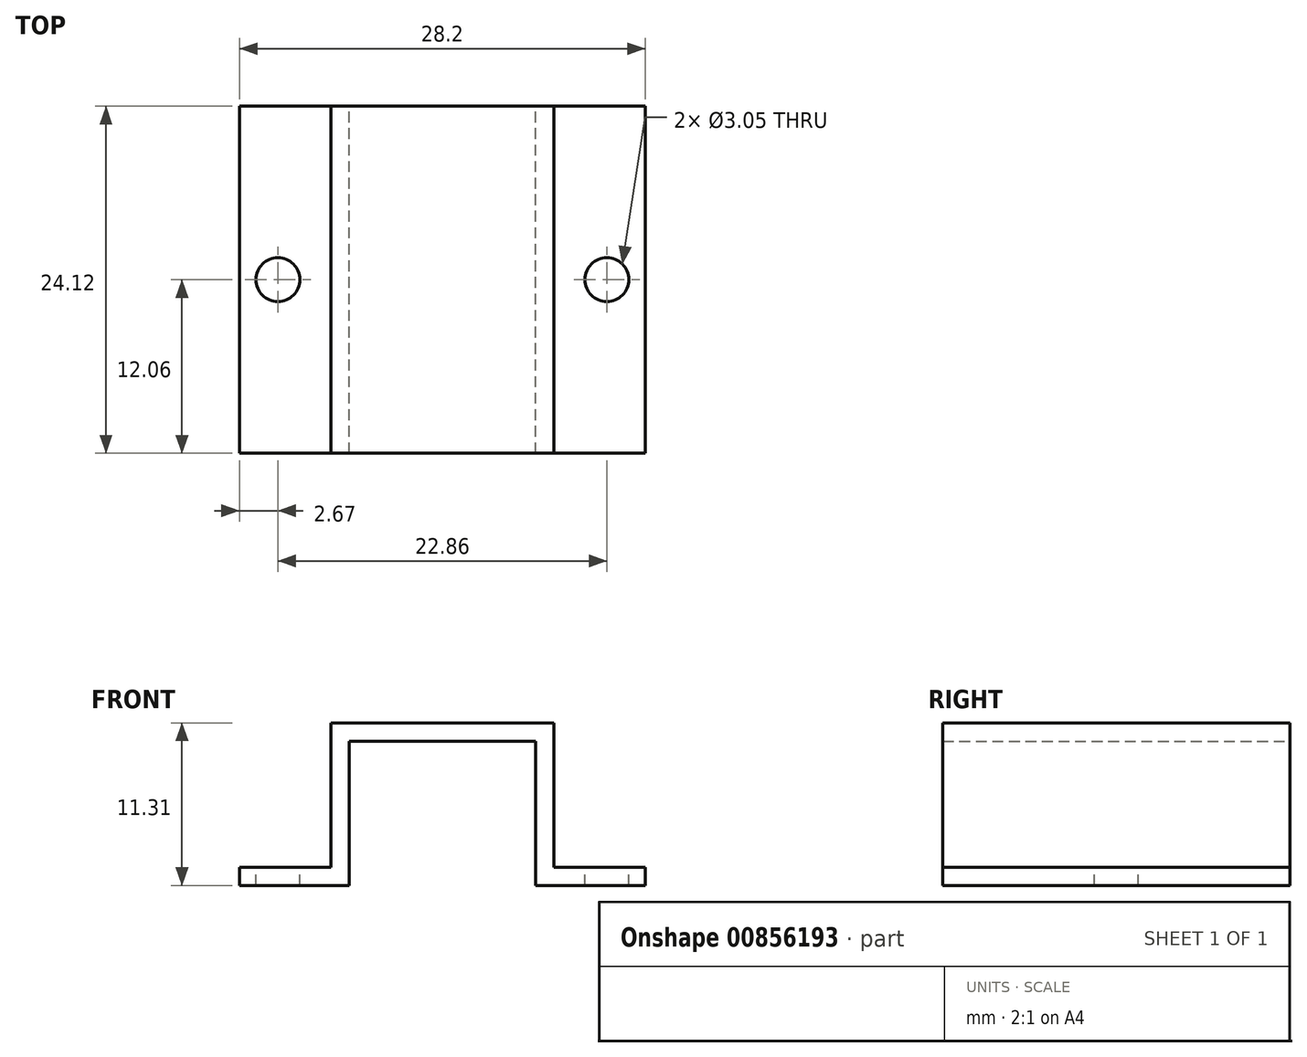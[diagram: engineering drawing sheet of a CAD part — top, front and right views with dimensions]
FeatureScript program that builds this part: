
annotation { "Feature Type Name" : "Feature", "Feature Type Description" : "" }
export const myFeature = defineFeature(function(context is Context, id is Id, definition is map)
    precondition{}
    {
        {
            var Q0;
            Q0=qCreatedBy(makeId("Front.planeOp"),FACE);
            var sketch = newSketch(context, id + "F0", { "sketchPlane" : qUnion([Q0])});
            skLineSegment(sketch, "E0.top", {"start": v(6.48, 5.02) * mm, "end": v(-6.48, 5.02) * mm});
            skLineSegment(sketch, "E0.left", {"start": v(6.48, -5.02) * mm, "end": v(6.48, 5.02) * mm});
            skLineSegment(sketch, "E0.right", {"start": v(-6.48, -5.02) * mm, "end": v(-6.48, 5.02) * mm});
            skPoint(sketch, "E0.middle", {"position": v(0, 0) * mm});
            skLineSegment(sketch, "E1.bottom", {"start": v(6.48, -5.02) * mm, "end": v(14.1, -5.02) * mm});
            skLineSegment(sketch, "E1.right", {"start": v(14.1, -5.02) * mm, "end": v(14.1, -3.75) * mm});
            skLineSegment(sketch, "E2.MirrorCS", {"start": v(-14.1, -5.02) * mm, "end": v(-14.1, -3.75) * mm});
            skLineSegment(sketch, "E3.MirrorCS", {"start": v(-6.48, -5.02) * mm, "end": v(-14.1, -5.02) * mm});
            skLineSegment(sketch, "E4", {"start": v(14.1, -3.75) * mm, "end": v(7.75, -3.75) * mm});
            skLineSegment(sketch, "E5", {"start": v(7.75, -3.75) * mm, "end": v(7.75, 6.29) * mm});
            skLineSegment(sketch, "E6", {"start": v(7.75, 6.29) * mm, "end": v(0, 6.29) * mm});
            skLineSegment(sketch, "E7.MirrorCS", {"start": v(-7.75, 6.29) * mm, "end": v(0, 6.29) * mm});
            skLineSegment(sketch, "E8.MirrorCS", {"start": v(-7.75, -3.75) * mm, "end": v(-7.75, 6.29) * mm});
            skLineSegment(sketch, "E9.MirrorCS", {"start": v(-14.1, -3.75) * mm, "end": v(-7.75, -3.75) * mm});
            skSolve(sketch);
        }
        {
            var Q0;
            Q0 = qSketchRegion(id + "F0", true);
            extrude(context, id + "F1", {"entities" : qUnion([Q0]), "depth" : 24.13 * mm, "offsetDistance" : 25.4 * mm, "symmetric" : true});
        }
        {
            var Q0;
            Q0=makeQuery(id+"F1.opExtrude","SWEPT_FACE",FACE,{"disambiguationData":[OSD([sQuery(id+"F0.wireOp",EDGE,"E9.MirrorCS")])]});
            var sketch = newSketch(context, id + "F2", { "sketchPlane" : qUnion([Q0])});
            skCircle(sketch, "E10", {"center": v(-11.43, 0) * mm, "radius": 1.52 * mm});
            skCircle(sketch, "E11.MirrorC", {"center": v(11.43, 0) * mm, "radius": 1.52 * mm});
            skSolve(sketch);
        }
        {
            var Q0;
            Q0 = qSketchRegion(id + "F2", true);
            extrude(context, id + "F3", {"entities" : qUnion([Q0]), "operationType" : NewBodyOperationType.REMOVE, "endBound" : BoundingType.UP_TO_NEXT, "oppositeDirection" : true, "depth" : 25.4 * mm, "offsetDistance" : 25.4 * mm});
        }
    });
